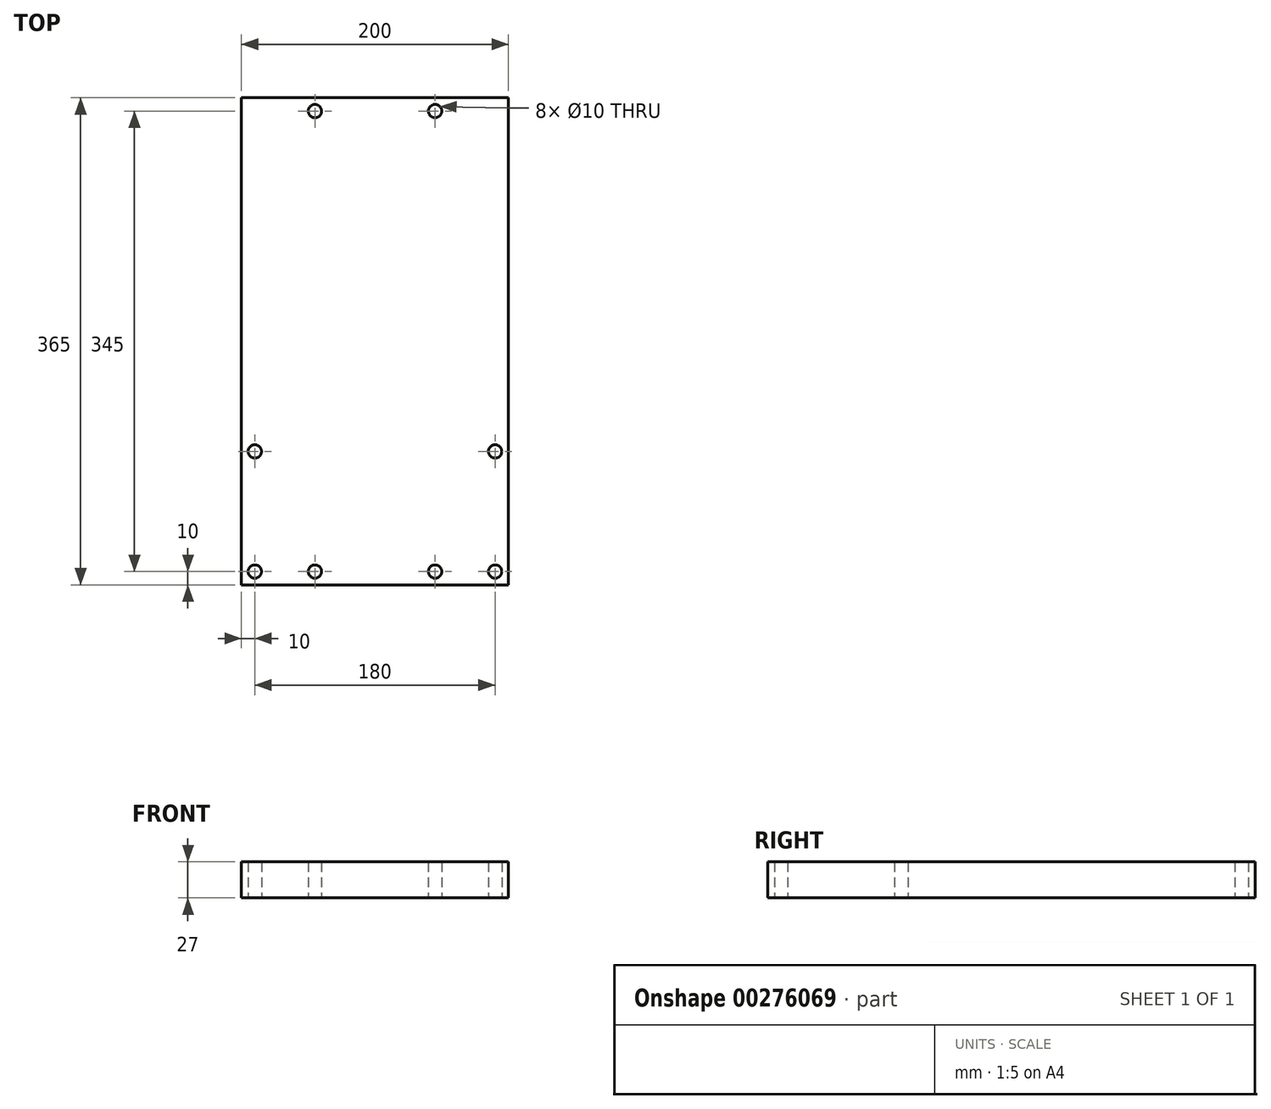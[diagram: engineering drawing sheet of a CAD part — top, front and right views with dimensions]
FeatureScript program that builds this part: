
annotation { "Feature Type Name" : "Feature", "Feature Type Description" : "" }
export const myFeature = defineFeature(function(context is Context, id is Id, definition is map)
    precondition{}
    {
        {
            var Q0;
            Q0=qCreatedBy(makeId("Top.planeOp"),FACE);
            var sketch = newSketch(context, id + "F0", { "sketchPlane" : qUnion([Q0])});
            skLineSegment(sketch, "E0.bottom", {"start": v(-100, 0) * mm, "end": v(100, 0) * mm});
            skLineSegment(sketch, "E0.top", {"start": v(-100, 365) * mm, "end": v(100, 365) * mm});
            skLineSegment(sketch, "E0.left", {"start": v(-100, 0) * mm, "end": v(-100, 365) * mm});
            skLineSegment(sketch, "E0.right", {"start": v(100, 0) * mm, "end": v(100, 365) * mm});
            skCircle(sketch, "E1", {"center": v(-90, 10) * mm, "radius": 5 * mm});
            skCircle(sketch, "E2", {"center": v(-90, 100) * mm, "radius": 5 * mm});
            skCircle(sketch, "E3", {"center": v(90, 100) * mm, "radius": 5 * mm});
            skCircle(sketch, "E4", {"center": v(90, 10) * mm, "radius": 5 * mm});
            skCircle(sketch, "E5", {"center": v(-45, 10) * mm, "radius": 5 * mm});
            skCircle(sketch, "E6", {"center": v(45, 10) * mm, "radius": 5 * mm});
            skCircle(sketch, "E7", {"center": v(-45, 355) * mm, "radius": 5 * mm});
            skCircle(sketch, "E8", {"center": v(45, 355) * mm, "radius": 5 * mm});
            skSolve(sketch);
        }
        {
            var Q0;
            Q0=makeQuery(id+"F0.imprint","IMPRINT",FACE,{"disambiguationData":[TD([[makeQuery(id+"F0.imprint","IMPRINT",EDGE,{"derivedFrom":sQuery(id+"F0.wireOp",EDGE,"E0.bottom")}),1.0]])]});
            extrude(context, id + "F1", {"entities" : qUnion([Q0]), "depth" : 27 * mm});
        }
    });
